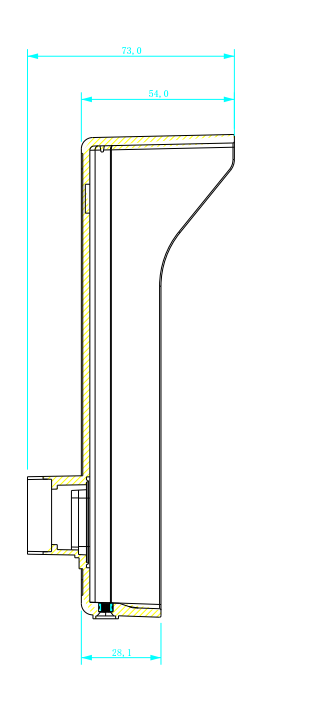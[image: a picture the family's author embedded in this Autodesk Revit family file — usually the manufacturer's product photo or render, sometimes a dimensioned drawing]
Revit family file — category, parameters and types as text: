
# Revit family: EVRC-IP
name_source: partatom
category: Устройства связи
units: mm (PartAtom-declared; Revit-internal decimal feet)

## family parameters
Всегда вертикально = Нет
На основе рабочей плоскости = Да
Общий = Да
При загрузке вырезать с полостями = Нет
Размер круглого соединителя = Использовать диаметр
Сохранять ориентацию аннотаций = Нет
Тип детали = Нормальный
Точка принадлежности помещению = Нет

## types (1)
- EVRC-IP
    ADSK_URL документации изделия = http://cdn.bas-ip.com
    ADSK_URL страницы изделия = https://www.bas-ip.ru
    ADSK_Версия Revit = Revit 2020
    ADSK_Единица измерения = шт
    ADSK_Завод-изготовитель = BAS-IP
    ADSK_Классификация нагрузок = Модуль IP управления лифтом
    ADSK_Количество фаз = 1
    ADSK_Коэффициент мощности = 1
    ADSK_Марка = EVRC-IP
    ADSK_Наименование = Модуль IP управления лифтом EVRC-IP
    ADSK_Наименование краткое = EVRC-IP
    ADSK_Напряжение = 24 В
    ADSK_Номинальная мощность = 7 Вт
    ADSK_Полная мощность = 7 В·А
    ADSK_Размер_Длина = 196 мм
    ADSK_Размер_Толщина = 37 мм
    ADSK_Размер_Ширина = 116 мм
    BIM library = https://bimlib.ru
    URL = https://www.bas-ip.ru
    Габаритные размеры = 195.5×116×37 мм
    Группа модели = Модуль IP управления лифтом EVRC-IP
    Изготовитель = BAS-IP
    Изображение типоразмера = <Нет>
    Максимальное количество модулей в одной системе = 98
    Описание = Модуль IP управления лифтом EVRC-IP - Контроллер предназначен для управления 16-ю каналами, путем подключения сухих контактов от EVRC-IP на контакты контроллеров автоматизации зданий.

Модуль имеет поддержку питания по PoE и позволяет организовать доступ в помещения или кабину при вызове с вызывной панели, либо же при поднесении бесконтактной карты.

У модуля есть два интерфейса взаимодействия: RS-485 (опционально) и Ethernet. По этим интерфейсам модуль получает информацию о поднесенной карте или введенном коде, и исходя из этого выдает различные права доступа для использования жильцами.

Также к контроллеру можно подключить контакты от пожарной сигнализации для блокировки кабины в случае пожара.

Данный контроллер может применяться в различных системах автоматизации зданий по усмотрению заказчика, например, в качестве контроллера управления лифтовым оборудованием
    Отметка по умолчанию = 0 мм
    Относительная влажность хранения = 20%-90%
    Потребляемая мощность в работе = 7 Ватт
    Потребляемая мощность в режиме ожидания = 1 Ватт
    Потребляемое напряжение = PoE 802.3af
    Температурный режим = -40 – +70 C
